# Revit family: Layout-Teknion-Zones_Open_Lounge_01-R2022
name_source: partatom
category: Furniture Systems
units: mm (PartAtom-declared; Revit-internal decimal feet)

## family parameters
Always vertical = Yes
Cut with Voids When Loaded = No
OmniClass Number = 23.40.70.14.64.21
OmniClass Title = Systems Furniture
Part Type = Normal
Room Calculation Point = No
Round Connector Dimension = Use Diameter
Shared = No
Work Plane-Based = No

## types (1)
- Open Lounge 01
    Apparent Load = 21 VA
    Apparent Load Note = With Floor Lamp = 21 VA - Without Floor Lamp = 0 V
    Assembly Code = E2020200
    Connector Description = Power Connector
    Default Elevation = 0' - 0"
    Depth = 7' - 4"
    Description = 9'-3" x 7'-2" Overall
    Height = 5' - 7"
    Manufacturer = Teknion
    Manufacturer Fax = 416.661.4586
    Model = Open Lounge Zone 01
    Product Line = Zones
    Product Page URL = http://teknionplanningtool.com
    Series = Zones
    Sustainability Data = http://www.teknion.com
    URL = http://www.teknion.com
    Voltage = 120 V
    Voltage Note = With Floor Lamp = 120 V - Without Floor Lamp = 0 V
    Warranty = http://www.teknion.com
    Width = 10' - 7"

## geometry (parser evidence)
native form markers: Blend x94, Sweep x24
no freeform markers — native parametric forms only
